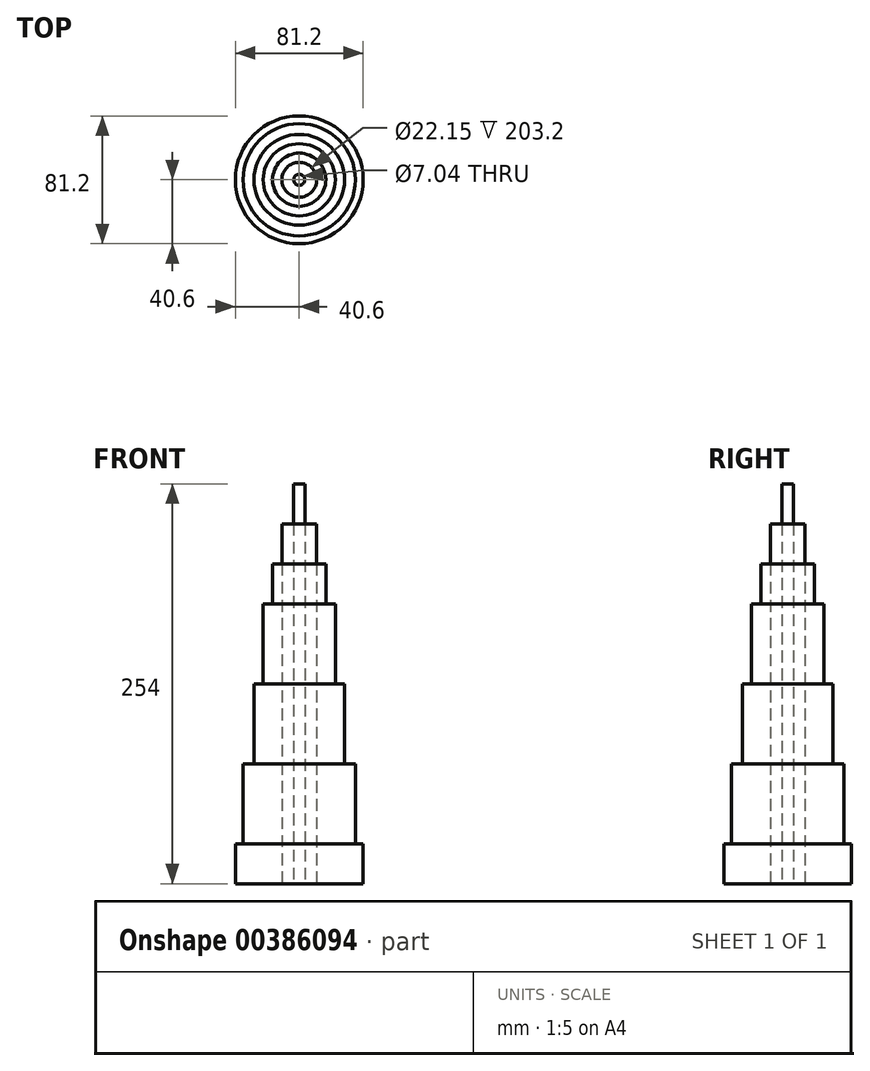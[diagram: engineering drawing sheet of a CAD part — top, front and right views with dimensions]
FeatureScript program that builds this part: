
annotation { "Feature Type Name" : "Feature", "Feature Type Description" : "" }
export const myFeature = defineFeature(function(context is Context, id is Id, definition is map)
    precondition{}
    {
        {
            var Q0;
            Q0=qCreatedBy(makeId("Top.planeOp"),FACE);
            var sketch = newSketch(context, id + "F0", { "sketchPlane" : qUnion([Q0])});
            skCircle(sketch, "E0", {"center": v(0, 0) * mm, "radius": 40.6 * mm});
            skCircle(sketch, "E1", {"center": v(0, 0) * mm, "radius": 35.67 * mm});
            skCircle(sketch, "E2", {"center": v(0, 0) * mm, "radius": 28.8 * mm});
            skCircle(sketch, "E3", {"center": v(0, 0) * mm, "radius": 22.92 * mm});
            skCircle(sketch, "E4", {"center": v(0, 0) * mm, "radius": 16.9 * mm});
            skCircle(sketch, "E5", {"center": v(0, 0) * mm, "radius": 11.08 * mm});
            skCircle(sketch, "E6", {"center": v(0, 0) * mm, "radius": 3.52 * mm});
            skSolve(sketch);
        }
        {
            var Q0;
            Q0=makeQuery(id+"F0.imprint","IMPRINT",FACE,{"disambiguationData":[TD([[makeQuery(id+"F0.imprint","IMPRINT",EDGE,{"derivedFrom":sQuery(id+"F0.wireOp",EDGE,"E6")}),1.0]])]});
            extrude(context, id + "F1", {"entities" : qUnion([Q0]), "depth" : 254 * mm});
        }
        {
            var Q0;
            Q0 = qSketchRegion(id + "F0", true);
            extrude(context, id + "F2", {"entities" : qUnion([Q0]), "depth" : 25.4 * mm});
        }
        {
            var Q0;
            Q0=makeQuery(id+"F0.imprint","IMPRINT",FACE,{"disambiguationData":[TD([[makeQuery(id+"F0.imprint","IMPRINT",EDGE,{"derivedFrom":sQuery(id+"F0.wireOp",EDGE,"E1")}),1.0]])]});
            extrude(context, id + "F3", {"entities" : qUnion([Q0]), "operationType" : NewBodyOperationType.ADD, "depth" : 76.2 * mm});
        }
        {
            var Q0;
            Q0=makeQuery(id+"F0.imprint","IMPRINT",FACE,{"disambiguationData":[TD([[makeQuery(id+"F0.imprint","IMPRINT",EDGE,{"derivedFrom":sQuery(id+"F0.wireOp",EDGE,"E2")}),1.0]])]});
            extrude(context, id + "F4", {"entities" : qUnion([Q0]), "operationType" : NewBodyOperationType.ADD, "depth" : 127 * mm});
        }
        {
            var Q0;
            Q0=makeQuery(id+"F0.imprint","IMPRINT",FACE,{"disambiguationData":[TD([[makeQuery(id+"F0.imprint","IMPRINT",EDGE,{"derivedFrom":sQuery(id+"F0.wireOp",EDGE,"E3")}),1.0]])]});
            extrude(context, id + "F5", {"entities" : qUnion([Q0]), "operationType" : NewBodyOperationType.ADD, "depth" : 177.8 * mm});
        }
        {
            var Q0;
            Q0=makeQuery(id+"F0.imprint","IMPRINT",FACE,{"disambiguationData":[TD([[makeQuery(id+"F0.imprint","IMPRINT",EDGE,{"derivedFrom":sQuery(id+"F0.wireOp",EDGE,"E4")}),1.0]])]});
            extrude(context, id + "F6", {"entities" : qUnion([Q0]), "operationType" : NewBodyOperationType.ADD, "depth" : 203.2 * mm});
        }
        {
            var Q0;
            Q0=makeQuery(id+"F0.imprint","IMPRINT",FACE,{"disambiguationData":[TD([[makeQuery(id+"F0.imprint","IMPRINT",EDGE,{"derivedFrom":sQuery(id+"F0.wireOp",EDGE,"E5")}),1.0]])]});
            extrude(context, id + "F7", {"entities" : qUnion([Q0]), "depth" : 228.6 * mm});
        }
        {
            var Q0;
            Q0=qCreatedBy(makeId("Top.planeOp"),FACE);
            var sketch = newSketch(context, id + "F8", { "sketchPlane" : qUnion([Q0])});
            skFitSpline(sketch, "E7", {"points": [v(5.6, -56.26) * mm, v(7.34, -59.35) * mm, v(9.93, -59.67) * mm, v(10.46, -61.41) * mm, v(12.51, -61.43) * mm, v(13.6, -58.8) * mm, v(17.4, -60.7) * mm, v(19.9, -64.76) * mm, v(23.38, -66.89) * mm, v(25.92, -62.2) * mm, v(28, -64.83) * mm, v(33.05, -59.35) * mm, v(38.46, -65.54) * mm, v(50.53, -59.49) * mm, v(61.84, -61.48) * mm, v(64.74, -63.22) * mm, v(65.9, -61.86) * mm, v(68.22, -62.64) * mm, v(72.28, -66.5) * mm, v(74.99, -66.5) * mm, v(75.82, -56.93) * mm, v(75.84, -56.33) * mm], "startDerivative": vector(23.93, -96.64) * mm, "endDerivative": vector(0, 73) * mm});
            skLineSegment(sketch, "E8", {"start": v(5.6, -56.26) * mm, "end": v(75.84, -56.33) * mm});
            skLineSegment(sketch, "E9", {"start": v(-27.09, 39.29) * mm, "end": v(-76.66, 49.05) * mm});
            skFitSpline(sketch, "E10", {"points": [v(-27.09, 39.29) * mm, v(-27.09, 42.8) * mm, v(-27.09, 44.55) * mm], "startDerivative": vector(0, 5.26) * mm, "endDerivative": vector(0, 5.26) * mm});
            skSolve(sketch);
        }
        {
            var Q0;
            Q0=sQuery(id+"F8.wireOp",EDGE,"E7");
            var Q1;
            Q1=sQuery(id+"F8.wireOp",EDGE,"E8");
            revolve(context, id + "F9", {"bodyType" : ToolBodyType.SURFACE, "surfaceEntities" : qUnion([Q0]), "axis" : qUnion([Q1]), "revolveType" : RevolveType.FULL});
        }
    });
